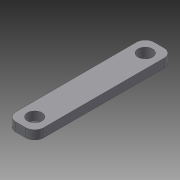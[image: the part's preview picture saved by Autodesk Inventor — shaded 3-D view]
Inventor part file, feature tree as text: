
AUTODESK INVENTOR PART (.ipt)
format: ipt  version: 2015 (Build 190159000, 159)  size: 94,208 bytes
history: native  units: in
note: dims shown in document units (in); Inventor stores cm internally (conversion verified against a paired STEP export)
features: extrude x1, sketch x1
ambient origin geometry x8: Origin, YZ Plane, XZ Plane, XY Plane, X Axis, Y Axis, Z Axis, Center Point
bodies: Solid1 (feature_tree)
feature tree (2):
  extrude  "Extrusion1"  Depth=0.7874in
  sketch  "Sketch1"  dims[d0=3.937in d1=0.7874in d2=0.4134in d3=3.1496in d4=0.25in d5=0.25in d6=0.0in]
